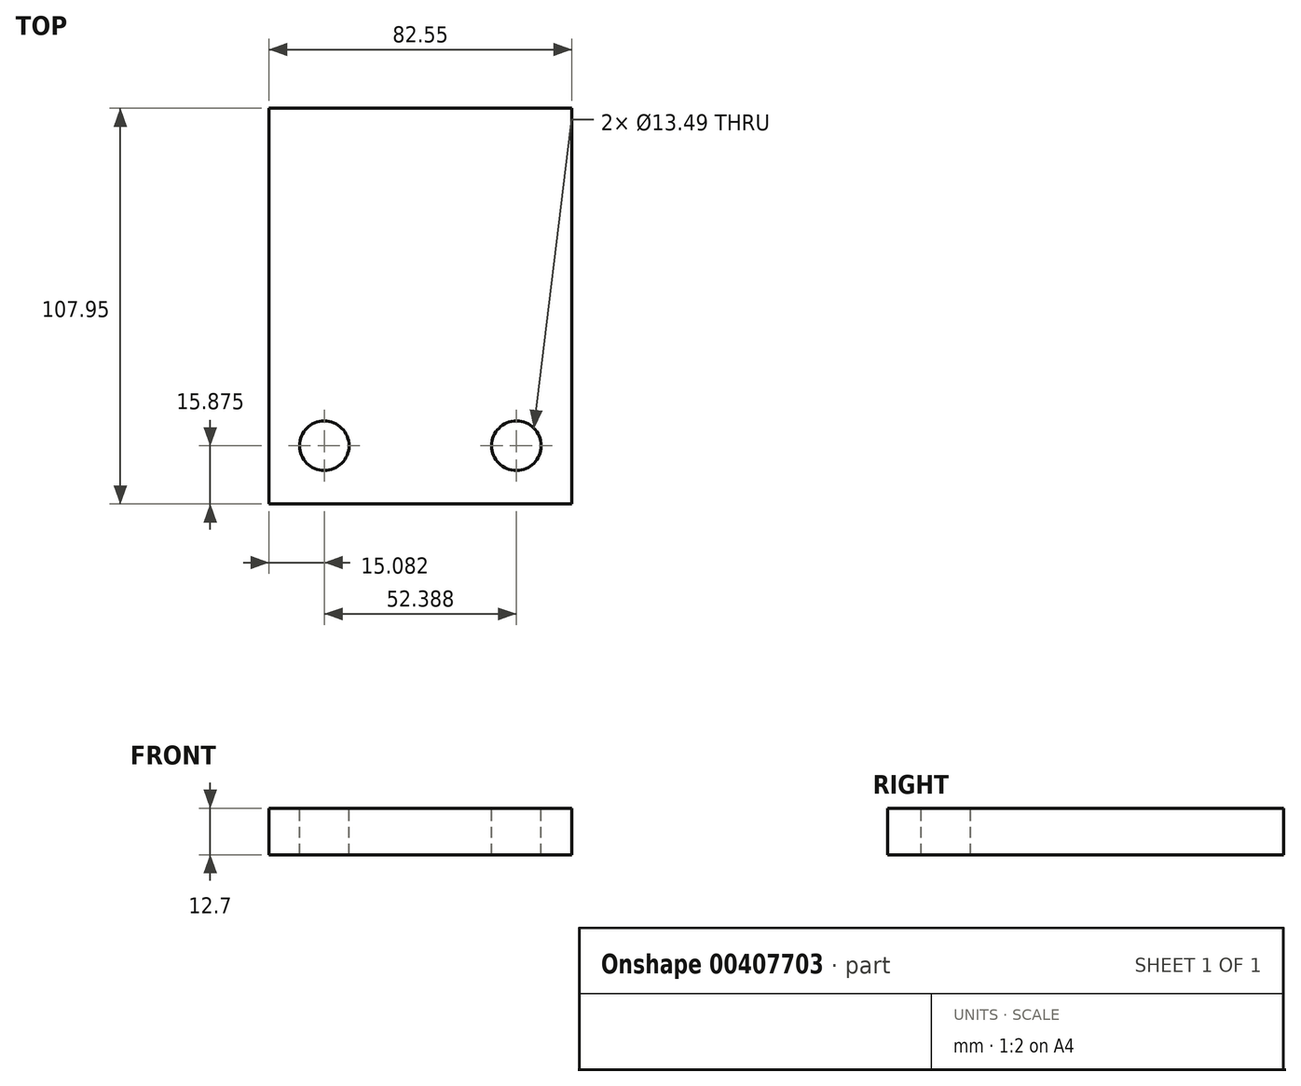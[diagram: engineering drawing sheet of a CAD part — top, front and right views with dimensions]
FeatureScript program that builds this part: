
annotation { "Feature Type Name" : "Feature", "Feature Type Description" : "" }
export const myFeature = defineFeature(function(context is Context, id is Id, definition is map)
    precondition{}
    {
        {
            var Q0;
            Q0=qCreatedBy(makeId("Top.planeOp"),FACE);
            var sketch = newSketch(context, id + "F0", { "sketchPlane" : qUnion([Q0])});
            skLineSegment(sketch, "E0.bottom", {"start": v(-29.43, 50.8) * mm, "end": v(53.12, 50.8) * mm});
            skLineSegment(sketch, "E0.top", {"start": v(-29.43, -57.15) * mm, "end": v(53.12, -57.15) * mm});
            skLineSegment(sketch, "E0.left", {"start": v(-29.43, 50.8) * mm, "end": v(-29.43, -57.15) * mm});
            skLineSegment(sketch, "E0.right", {"start": v(53.12, 50.8) * mm, "end": v(53.12, -57.15) * mm});
            skSolve(sketch);
        }
        {
            var Q0;
            Q0 = qSketchRegion(id + "F0", true);
            extrude(context, id + "F1", {"entities" : qUnion([Q0]), "depth" : 12.7 * mm});
        }
        {
            var Q0;
            Q0=makeQuery(id+"F1.opExtrude","CAP_FACE",FACE,{"disambiguationData":[OSD([sQuery(id+"F0.wireOp",EDGE,"E0.bottom"),sQuery(id+"F0.wireOp",EDGE,"E0.top"),sQuery(id+"F0.wireOp",EDGE,"E0.left"),sQuery(id+"F0.wireOp",EDGE,"E0.right")])],"isStart":false});
            var sketch = newSketch(context, id + "F2", { "sketchPlane" : qUnion([Q0])});
            skCircle(sketch, "E1", {"center": v(-14.35, -41.27) * mm, "radius": 6.35 * mm});
            skCircle(sketch, "E2", {"center": v(38.04, -41.27) * mm, "radius": 6.35 * mm});
            skSolve(sketch);
        }
        {
            var Q0;
            Q0=sQuery(id+"F2.wireOp",VERTEX,"E1.center");
            var Q1;
            Q1=sQuery(id+"F2.wireOp",VERTEX,"E2.center");
            var Q2;
            Q2=makeQuery(id+"F1.opExtrude","SWEPT_BODY",BODY,{"disambiguationData":[OSD([sQuery(id+"F0.wireOp",EDGE,"E0.bottom"),sQuery(id+"F0.wireOp",EDGE,"E0.top"),sQuery(id+"F0.wireOp",EDGE,"E0.left"),sQuery(id+"F0.wireOp",EDGE,"E0.right")])]});
            hole(context, id + "F3", {"style" : HoleStyle.SIMPLE, "endStyle" : HoleEndStyle.THROUGH, "standardTappedOrClearance" : lookupTablePath({ "standard" : "ANSI", "fit" : "Normal (ASME)", "size" : "1/2", "type" : "Clearance" }), "standardBlindInLast" : lookupTablePath({ "fit" : "Free", "standard" : "ANSI", "size" : "1/2", "type" : "Clearance" }), "holeDiameter" : 13.5 * mm, "isTappedThrough" : true, "tappedDepth" : 12.7 * mm, "tapClearance" : 3, "locations" : qUnion([Q0, Q1]), "scope" : qUnion([Q2])});
        }
    });
